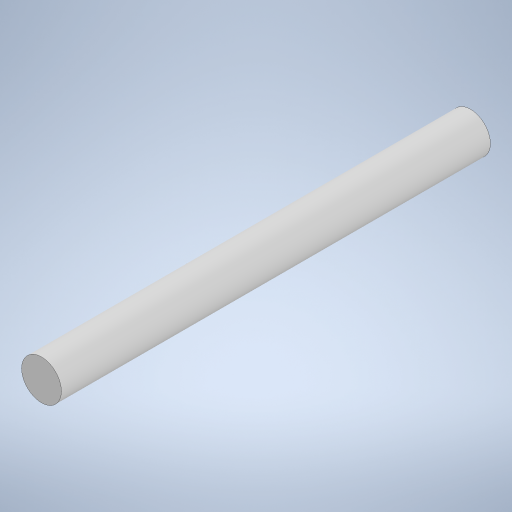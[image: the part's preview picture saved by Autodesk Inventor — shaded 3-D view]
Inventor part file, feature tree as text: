
AUTODESK INVENTOR PART (.ipt)
format: ipt  version: 2023 (Build 270158000, 158)  size: 225,280 bytes
history: native  units: in
note: dims shown in document units (in); Inventor stores cm internally (conversion verified against a paired STEP export)
features: extrude x1, sketch x1
ambient origin geometry x8: Origin, YZ Plane, XZ Plane, XY Plane, X Axis, Y Axis, Z Axis, Center Point
bodies: Solid1 (feature_tree)
feature tree (2):
  extrude  "Extrusion1"  Depth=27.0in TaperAngle=0.0deg
  sketch  "Sketch1"  dims[d0=2.5in d1=27.0in d2=0.0in]
